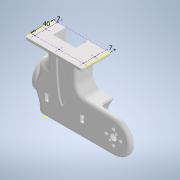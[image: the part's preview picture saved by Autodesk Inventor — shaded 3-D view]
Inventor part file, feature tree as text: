
AUTODESK INVENTOR PART (.ipt)
format: ipt  version: 2020 (Build 240168000, 168)  size: 967,168 bytes
history: native  units: mm
features: sketch x28, fillet x24, extrude x18, hole x7, other x6, reference x4, shell x1, projected_geometry x1
ambient origin geometry x8: Origin, YZ Plane, XZ Plane, XY Plane, X Axis, Y Axis, Z Axis, Center Point
bodies: Solid1 (feature_tree)
feature tree (89):
  extrude  "Extrusion1"  Depth=58.0mm
  shell  "Shell1"  Thickness=15.0mm
  extrude  "Extrusion2"  Depth=30.0mm
  extrude  "Extrusion3"  Depth=120.0mm
  hole  "Hole1"  [1 undecoded]
  extrude  "Extrusion5"  Depth=60.0mm
  hole  "Hole2"  [1 undecoded]
  extrude  "Extrusion6"  Depth=40.0mm
  extrude  "Extrusion7"  TaperAngle=0.0deg  [1 undecoded]
  extrude  "Extrusion8"  Depth=2.0mm
  fillet  "Fillet1"  Radius=2.0mm
  fillet  "Fillet2"  [1 undecoded]
  fillet  "Fillet4"  Radius=20.0mm
  fillet  "Fillet5"  Radius=81.0mm
  fillet  "Fillet7"  [1 undecoded]
  fillet  "Fillet10"  [1 undecoded]
  fillet  "Fillet11"  Radius=25.0mm
  fillet  "Fillet13"  Radius=3.4mm
  extrude  "Extrusion9"  TaperAngle=90.0deg  [1 undecoded]
  hole  "Hole3"  [1 undecoded]
  fillet  "Fillet15"  [1 undecoded]
  fillet  "Fillet16"  [1 undecoded]
  extrude  "Extrusion12"  Depth=90.0mm
  extrude  "Extrusion13"  Depth=12.0mm
  extrude  "Extrusion14"  Depth=10.0mm TaperAngle=0.0deg
  fillet  "Fillet17"  Radius=2.0mm
  fillet  "Fillet18"  Radius=18.0mm
  fillet  "Fillet19"  Radius=10.0mm
  fillet  "Fillet21"  Radius=18.0mm
  extrude  "Extrusion15"  Depth=4.0mm
  fillet  "Fillet24"  Radius=4.0mm
  fillet  "Fillet25"  Radius=7.0mm
  fillet  "Fillet26"  Radius=12.0mm
  fillet  "Fillet27"  Radius=5.5mm
  hole  "Hole6"  [1 undecoded]
  hole  "Hole7"  [1 undecoded]
  fillet  "Fillet28"  Radius=25.0mm
  sketch  "Sketch29"  dims[d114=5.0mm d115=3.0mm d116=0.0mm d117=25.0mm]
  extrude  "Extrusion16"  Depth=20.0mm TaperAngle=0.0deg
  hole  "Hole8"  [1 undecoded]
  extrude  "Extrusion17"  Depth=12.0mm
  extrude  "Extrusion18"  Depth=3.0mm
  hole  "Hole10"  [1 undecoded]
  extrude  "Extrusion19"  Depth=10.0mm TaperAngle=0.0deg
  fillet  "Fillet29"  Radius=10.0mm
  fillet  "Fillet30"  Radius=3.0mm
  sketch  "Sketch38"  dims[d146=3.0mm]
  sketch  "Sketch39"  dims[d147=3.4mm d148=15.875mm d149=11.0mm d150=2.6mm d151=90.0deg d152=8.0mm d153=0.0mm d154=40.0mm]
  fillet  "Fillet38"  Radius=3.0mm
  extrude  "Extrusion21"  Depth=40.0mm
  fillet  "Fillet39"  Radius=3.0mm
  extrude  "Extrusion22"  Depth=2.0mm TaperAngle=0.0deg
  fillet  "Fillet40"  Radius=7.0mm
  sketch  "Sketch1"  dims[d4=54.0mm d6=58.0mm d7=15.0mm]
  sketch  "Sketch3"  dims[d8=65.0mm d9=30.0mm]
  sketch  "Sketch4"  dims[d10=0.0mm d12=120.0mm]
  sketch  "Sketch5"  dims[d14=15.0mm d15=80.0mm]
  sketch  "Sketch7"  dims[d16=52.0mm d17=60.0mm]
  sketch  "Sketch8"  dims[d19=24.0mm d20=0.0mm]
  sketch  "Sketch9"  dims[d21=7.0mm d22=40.0mm]
  sketch  "Sketch10"  dims[d23=20.0mm d24=0.0mm]
  sketch  "Sketch11"  dims[d25=25.0mm d26=3.4mm d27=6.0mm d28=6.3mm d29=2.0mm d30=90.0deg d31=20.0mm d32=0.0mm d46=81.0mm d47=0.0mm d48=0.0mm d49=25.0mm d50=3.4mm d51=6.0mm]
  sketch  "Sketch13"  dims[d52=6.3mm d53=2.0mm d54=90.0deg]
  sketch  "Sketch16"  dims[d55=20.0mm d56=0.0mm d57=11.0mm d58=0.0mm d59=0.0mm]
  sketch  "Sketch20"  dims[d60=81.0mm d61=90.0mm]
  sketch  "Sketch22"  dims[d62=24.0mm d63=0.0mm d64=12.0mm]
  sketch  "Sketch23"  dims[d65=6.0mm d66=24.0mm d67=0.0mm d68=2.0mm d69=18.0mm d71=10.0mm d72=18.0mm]
  sketch  "Sketch24"  dims[d74=8.0mm d77=4.0mm d78=4.0mm d80=7.0mm d81=12.0mm d82=5.5mm]
  projected_geometry  "Projected Loop2"
  sketch  "Sketch26"  dims[d83=24.0mm d84=0.0mm]
  sketch  "Sketch28"  dims[d89=4.0mm d90=6.0mm d91=6.3mm d92=2.0mm d93=90.0deg d94=8.0mm d95=0.0mm d113=7.0mm]
  sketch  "Sketch30"  dims[d118=7.0mm d119=20.0mm d120=0.0mm]
  reference  "Reference1"
  reference  "Reference2"
  sketch  "Sketch31"  dims[d121=7.0mm d122=20.0mm]
  sketch  "Sketch32"  dims[d123=15.0mm d124=0.0mm d125=12.0mm]
  sketch  "Sketch33"  dims[d126=12.0mm d127=3.0mm]
  reference  "Reference3"
  reference  "Reference4"
  sketch  "Sketch36"  dims[d129=37.0mm d130=10.0mm]
  sketch  "Sketch37"  dims[d131=50.0mm d132=6.0mm d133=0.0mm d143=10.0mm d144=3.0mm d145=3.0mm]
  sketch  "Sketch41"  dims[d155=3.4mm d156=15.875mm d157=6.3mm d158=2.6mm d159=90.0deg d160=8.0mm d161=0.0mm d162=3.0mm]
  sketch  "Sketch42"  dims[d163=4.0mm d164=2.0mm d165=0.0mm d166=2.4mm d167=5.0mm d168=4.4mm d169=2.0mm d170=90.0deg d171=5.0mm d172=20.594885mm d173=7.0mm d174=105.185mm d175=0.0mm d183=7.0mm d184=2.0mm d185=0.0mm d186=2.4mm d187=5.0mm d188=4.4mm d189=2.0mm d190=90.0deg d191=5.0mm d192=20.594885mm d193=4.0mm d194=4.5mm d195=0.0mm d196=5.0mm d197=4.0mm d199=7.0mm d200=7.0mm d216=5.0mm d217=30.0mm d218=105.0mm d219=72.0mm d220=9.5mm d221=7.0mm d222=1.5mm d223=0.0mm d224=2.0mm d225=15.0mm d226=10.0mm d227=37.0mm d228=15.0mm d229=2.0mm d230=0.0mm d231=2.0mm]
  other  "<userpath>\Desktop\Robot_Project\Kang-BalancingRobot\Hardware\Cad\KangKang.iam"
  other  "KangKang.iam"
  other  "AS5147_ENC_ANGLE_VER01:1"
  other  "Board_86"
  other  "AS5147_ENC_VERTICAL_VER01:1"
  other  "Board_107"
note: 14 required parameter values undecoded (feature->parameter linkage not recoverable at this tier; creation-order binding heuristic only, values carry confidence <= 0.55)
